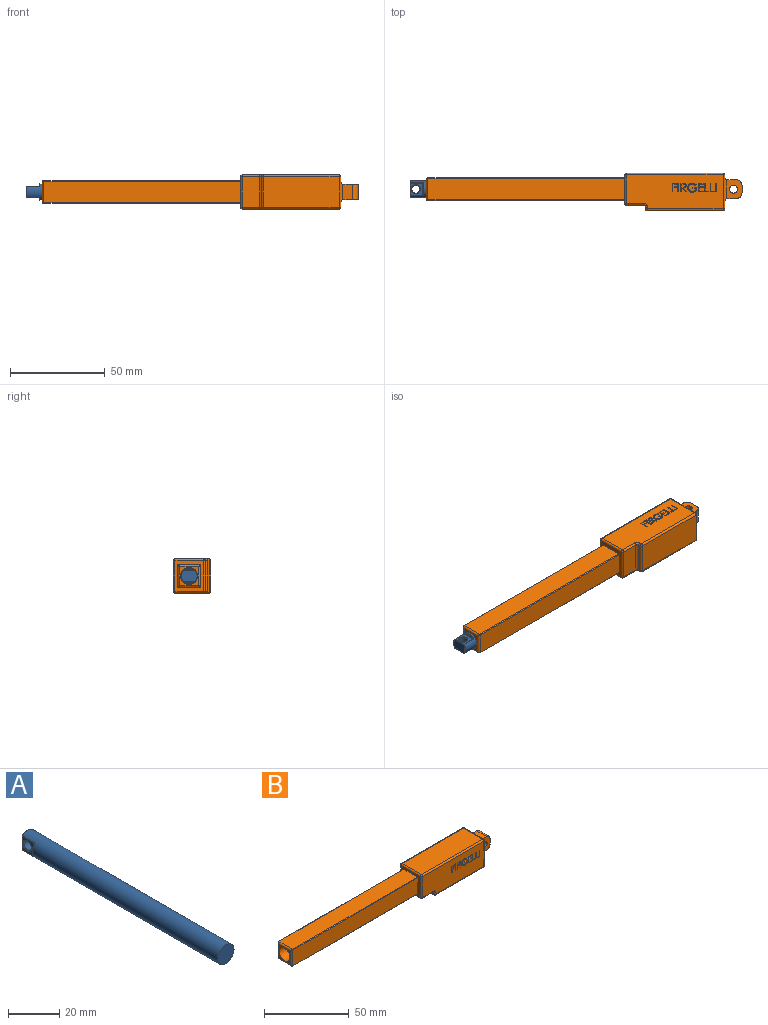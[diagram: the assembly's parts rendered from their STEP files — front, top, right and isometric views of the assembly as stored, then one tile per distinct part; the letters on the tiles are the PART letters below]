
ASSEMBLY  parts=2 mates=1
PART A: 30 faces, bbox 9.7x110x9.7 mm
  f0: cylinder r=4.5mm len=109.7mm, axis (0,-1,0), area 2992.2mm2, adj f2,f8,f9,f11,f13,f14,f15,f17
  f1: plane 8.4x5.4mm, normal (0,1,0), area 42mm2, adj f15,f16,f23,f24
  f2: plane 9x9mm, normal (0,-1,0), area 63.6mm2, adj f0
  f3: plane 6.43x6.4mm, normal (1,0,0), area 22.7mm2, adj f9,f10,f16,f17,f29
  f4: plane 5.2x0.9mm, normal (0,1,0), area 3.2mm2, adj f10,f11
  f5: plane 5.2x0.9mm, normal (0,1,0), area 3.2mm2, adj f21,f22
  f6: plane 6.43x6.4mm, normal (-1,0,0), area 22.7mm2, adj f14,f22,f23,f27,f28
  f7: cylinder r=2.12mm len=5.4mm, axis (1,0,0), area 72.1mm2, adj f28,f29
  f8: bspline ~0.85x0.71mm, area 0.3mm2, adj f0,f9,f10,f11
  f9: cylinder r=0.3mm len=6.4mm, axis (0,-1,0), area 1.7mm2, adj f0,f3,f8,f12
  f10: cylinder r=0.3mm len=6.43mm, axis (0,0,1), area 2.8mm2, adj f3,f4,f8,f13
  f11: torus R=4.2mm, axis (0,1,0), area 2.8mm2, adj f0,f4,f8,f13
  f12: sphere r=0.3mm, area 0.1mm2, adj f9,f15,f16
  f13: bspline ~1.14x0.87mm, area 0.3mm2, adj f0,f10,f11,f17
  f14: cylinder r=0.3mm len=6.4mm, axis (0,-1,0), area 1.7mm2, adj f0,f6,f18,f19
  f15: torus R=4.2mm, axis (0,1,0), area 2.9mm2, adj f0,f1,f12,f19
  f16: cylinder r=0.3mm len=6.43mm, axis (0,0,-1), area 3mm2, adj f1,f3,f12,f20
  f17: cylinder r=0.3mm len=6.4mm, axis (0,-1,0), area 1.7mm2, adj f0,f3,f13,f20
  f18: bspline ~1.14x0.87mm, area 0.3mm2, adj f0,f14,f21,f22
  f19: sphere r=0.3mm, area 0.1mm2, adj f14,f15,f23
  f20: sphere r=0.3mm, area 0.1mm2, adj f16,f17,f24
  f21: torus R=4.2mm, axis (0,1,0), area 2.8mm2, adj f0,f5,f18,f25
  f22: cylinder r=0.3mm len=6.43mm, axis (0,0,-1), area 2.8mm2, adj f5,f6,f18,f25
  f23: cylinder r=0.3mm len=6.43mm, axis (0,0,1), area 3mm2, adj f1,f6,f19,f26
  f24: torus R=4.2mm, axis (0,1,0), area 2.9mm2, adj f0,f1,f20,f26
  f25: bspline ~0.85x0.71mm, area 0.3mm2, adj f0,f21,f22,f27
  f26: sphere r=0.3mm, area 0.1mm2, adj f23,f24,f27
  f27: cylinder r=0.3mm len=6.4mm, axis (0,-1,0), area 1.7mm2, adj f0,f6,f25,f26
  f28: torus R=2.43mm, axis (-1,0,0), area 6.6mm2, adj f6,f7
  f29: torus R=2.43mm, axis (1,0,0), area 6.6mm2, adj f3,f7
PART B: 229 faces, bbox 167x18.2x20 mm
  f0: plane 51x18mm, normal (0,1,0), area 854.5mm2, adj f25,f31,f39,f40,f41,f43,f50,f149
  f1: plane 51x18mm, normal (0,-1,0), area 854.5mm2, adj f28,f36,f46,f53,f54,f55,f57,f69
  f2: cylinder r=1mm len=10mm, axis (0,-1,0), area 13.7mm2, adj f3,f19,f27,f30
  f3: plane 8x5mm, normal (0,0,1), area 40mm2, adj f2,f4,f26,f29
  f4: cylinder r=3mm len=8mm, axis (0,-1,0), area 37.7mm2, adj f3,f5,f26,f29
  f5: plane 8x4mm, normal (1,0,0), area 32mm2, adj f4,f6,f26,f29
  f6: cylinder r=3mm len=8mm, axis (0,-1,0), area 37.7mm2, adj f5,f7,f26,f29
  f7: plane 8x5mm, normal (0,0,-1), area 40mm2, adj f6,f8,f26,f29
  f8: cylinder r=1mm len=10mm, axis (0,-1,0), area 13.7mm2, adj f7,f19,f27,f30
  f9: cylinder r=1mm len=16mm, axis (0,-1,0), area 25.1mm2, adj f19,f20,f44,f58
  f10: cylinder r=1mm len=16mm, axis (0,-1,0), area 25.1mm2, adj f16,f24,f38,f52
  f11: plane 104x11.4mm, normal (0,0,-1), area 1185.6mm2, adj f12,f16,f65,f67
  f12: cylinder r=1mm len=11.4mm, axis (0,-1,0), area 17.1mm2, adj f11,f13,f66,f68
  f13: plane 10x10mm, normal (-1,0,0), area 36.4mm2, adj f12,f14,f33,f34,f59
  f14: cylinder r=1mm len=11.4mm, axis (0,-1,0), area 17.1mm2, adj f13,f15,f62,f64
  f15: plane 104x11.4mm, normal (0,0,1), area 1185.6mm2, adj f14,f16,f61,f63
  f16: plane 16x15mm, normal (-1,0,0), area 96.1mm2, adj f10,f11,f15,f17,f31,f32,f35,f36
  f17: cylinder r=1mm len=16mm, axis (0,-1,0), area 25.1mm2, adj f16,f18,f45,f51
  f18: plane 51x16mm, normal (0,0,1), area 816mm2, adj f17,f46,f48,f50
  f19: plane 18x16mm, normal (1,0,0), area 168mm2, adj f2,f8,f9,f25,f27,f28,f30,f48
  f20: plane 40x16mm, normal (0,0,-1), area 640mm2, adj f9,f21,f43,f57
  f21: cylinder r=1mm len=16mm, axis (0,-1,0), area 25.1mm2, adj f20,f22,f42,f56
  f22: plane 16x1mm, normal (-1,0,0), area 16mm2, adj f21,f23,f41,f55
  f23: cylinder r=1mm len=16mm, axis (0,-1,0), area 25.1mm2, adj f22,f24,f40,f54
  f24: plane 16x9mm, normal (0,0,-1), area 144mm2, adj f10,f23,f39,f53
  f25: cylinder r=1mm len=18mm, axis (0,0,1), area 28.3mm2, adj f0,f19,f44,f49
  f26: plane 10x8mm, normal (0,1,0), area 62mm2, adj f3,f4,f5,f6,f7,f27,f37
  f27: cylinder r=1mm len=12mm, axis (0,0,1), area 16.8mm2, adj f2,f8,f19,f26
  f28: cylinder r=1mm len=18mm, axis (0,0,1), area 28.3mm2, adj f1,f19,f47,f58
  f29: plane 10x8mm, normal (0,-1,0), area 62mm2, adj f3,f4,f5,f6,f7,f30,f37
  f30: cylinder r=1mm len=12mm, axis (0,0,1), area 16.8mm2, adj f2,f8,f19,f29
  f31: cylinder r=1mm len=15mm, axis (0,0,1), area 23.6mm2, adj f0,f16,f38,f51
  f32: plane 104x11.4mm, normal (0,1,0), area 1185.6mm2, adj f16,f33,f63,f67
  f33: cylinder r=1mm len=11.4mm, axis (0,0,1), area 17.1mm2, adj f13,f32,f64,f68
  f34: cylinder r=1mm len=11.4mm, axis (0,0,1), area 17.1mm2, adj f13,f35,f62,f66
  f35: plane 104x11.4mm, normal (0,-1,0), area 1185.6mm2, adj f16,f34,f61,f65
  f36: cylinder r=1mm len=15mm, axis (0,0,1), area 23.6mm2, adj f1,f16,f45,f52
  f37: cylinder r=2.12mm len=8mm, axis (0,-1,0), area 106.8mm2, adj f26,f29
  f38: sphere r=1mm, area 1.6mm2, adj f10,f31,f39
  f39: cylinder r=1mm len=9mm, axis (-1,0,0), area 14.1mm2, adj f0,f24,f38,f40
  f40: torus R=2mm, axis (0,-1,0), area 3.4mm2, adj f0,f23,f39,f41
  f41: cylinder r=1mm len=1mm, axis (0,0,1), area 1.6mm2, adj f0,f22,f40,f42
  f42: sphere r=1mm, area 1.6mm2, adj f21,f41,f43
  f43: cylinder r=1mm len=40mm, axis (-1,0,0), area 62.8mm2, adj f0,f20,f42,f44
  f44: sphere r=1mm, area 1.6mm2, adj f9,f25,f43
  f45: sphere r=1mm, area 1.6mm2, adj f17,f36,f46
  f46: cylinder r=1mm len=51mm, axis (-1,0,0), area 80.1mm2, adj f1,f18,f45,f47
  f47: sphere r=1mm, area 1.6mm2, adj f28,f46,f48
  f48: cylinder r=1mm len=16mm, axis (0,-1,0), area 25.1mm2, adj f18,f19,f47,f49
  f49: sphere r=1mm, area 1.6mm2, adj f25,f48,f50
  f50: cylinder r=1mm len=51mm, axis (1,0,0), area 80.1mm2, adj f0,f18,f49,f51
  f51: sphere r=1mm, area 1.6mm2, adj f17,f31,f50
  f52: sphere r=1mm, area 1.6mm2, adj f10,f36,f53
  f53: cylinder r=1mm len=9mm, axis (1,0,0), area 14.1mm2, adj f1,f24,f52,f54
  f54: torus R=2mm, axis (0,-1,0), area 3.4mm2, adj f1,f23,f53,f55
  f55: cylinder r=1mm len=1mm, axis (0,0,-1), area 1.6mm2, adj f1,f22,f54,f56
  f56: sphere r=1mm, area 1.6mm2, adj f21,f55,f57
  f57: cylinder r=1mm len=40mm, axis (1,0,0), area 62.8mm2, adj f1,f20,f56,f58
  f58: sphere r=1mm, area 1.6mm2, adj f9,f28,f57
  f59: cylinder r=4.5mm len=50mm, axis (-1,0,0), area 1413.7mm2, adj f13,f60
  f60: plane 9x9mm, normal (-1,0,0), area 63.6mm2, adj f59
  f61: cylinder r=0.3mm len=104mm, axis (1,0,0), area 49mm2, adj f15,f16,f35,f62
  f62: bspline ~1.17x1mm, area 0.5mm2, adj f14,f34,f61
  f63: cylinder r=0.3mm len=104mm, axis (-1,0,0), area 49mm2, adj f15,f16,f32,f64
  f64: bspline ~1.17x1mm, area 0.5mm2, adj f14,f33,f63
  f65: cylinder r=0.3mm len=104mm, axis (-1,0,0), area 49mm2, adj f11,f16,f35,f66
  f66: bspline ~1.04x1mm, area 0.5mm2, adj f12,f34,f65
  f67: cylinder r=0.3mm len=104mm, axis (1,0,0), area 49mm2, adj f11,f16,f32,f68
  f68: bspline ~1.17x1mm, area 0.5mm2, adj f12,f33,f67
  f69: plane 4.5x0.1mm, normal (-1,0,0), area 0.5mm2, adj f1,f70,f72,f73
  f70: plane 0.4x0.1mm, normal (0,0,-1), area 0mm2, adj f1,f69,f71,f73
  f71: plane 4.5x0.1mm, normal (1,0,0), area 0.5mm2, adj f1,f70,f72,f73
  f72: plane 0.4x0.1mm, normal (0,0,1), area 0mm2, adj f1,f69,f71,f73
  f73: plane 4.5x0.4mm, normal (0,-1,0), area 1.8mm2, adj f69,f70,f71,f72
  f74: plane 4.5x0.1mm, normal (-1,0,0), area 0.5mm2, adj f1,f75,f79,f80
  f75: plane 2.13x0.1mm, normal (0,0,-1), area 0.2mm2, adj f1,f74,f76,f80
  f76: plane 0.46x0.1mm, normal (1,0,0), area 0mm2, adj f1,f75,f77,f80
  f77: plane 1.73x0.1mm, normal (0,0,1), area 0.2mm2, adj f1,f76,f78,f80
  f78: plane 4.04x0.1mm, normal (1,0,0), area 0.4mm2, adj f1,f77,f79,f80
  f79: plane 0.4x0.1mm, normal (0,0,1), area 0mm2, adj f1,f74,f78,f80
  f80: plane 4.5x2.13mm, normal (0,-1,0), area 2.6mm2, adj f74,f75,f76,f77,f78,f79
  f81: plane 4.5x0.1mm, normal (-1,0,0), area 0.5mm2, adj f1,f82,f86,f87
  f82: plane 2.13x0.1mm, normal (0,0,-1), area 0.2mm2, adj f1,f81,f83,f87
  f83: plane 0.46x0.1mm, normal (1,0,0), area 0mm2, adj f1,f82,f84,f87
  f84: plane 1.73x0.1mm, normal (0,0,1), area 0.2mm2, adj f1,f83,f85,f87
  f85: plane 4.04x0.1mm, normal (1,0,0), area 0.4mm2, adj f1,f84,f86,f87
  f86: plane 0.4x0.1mm, normal (0,0,1), area 0mm2, adj f1,f81,f85,f87
  f87: plane 4.5x2.13mm, normal (0,-1,0), area 2.6mm2, adj f81,f82,f83,f84,f85,f86
  f88: plane 4.5x0.1mm, normal (-1,0,0), area 0.5mm2, adj f1,f89,f99,f100
  f89: plane 2.54x0.1mm, normal (0,0,-1), area 0.3mm2, adj f1,f88,f90,f100
  f90: plane 0.46x0.1mm, normal (1,0,0), area 0mm2, adj f1,f89,f91,f100
  f91: plane 2.13x0.1mm, normal (0,0,1), area 0.2mm2, adj f1,f90,f92,f100
  f92: plane 1.73x0.1mm, normal (1,0,0), area 0.2mm2, adj f1,f91,f93,f100
  f93: plane 2.13x0.1mm, normal (0,0,-1), area 0.2mm2, adj f1,f92,f94,f100
  f94: plane 0.46x0.1mm, normal (1,0,0), area 0mm2, adj f1,f93,f95,f100
  f95: plane 2.13x0.1mm, normal (0,0,1), area 0.2mm2, adj f1,f94,f96,f100
  f96: plane 1.38x0.1mm, normal (1,0,0), area 0.1mm2, adj f1,f95,f97,f100
  f97: plane 2.13x0.1mm, normal (0,0,-1), area 0.2mm2, adj f1,f96,f98,f100
  f98: plane 0.46x0.1mm, normal (1,0,0), area 0mm2, adj f1,f97,f99,f100
  f99: plane 2.54x0.1mm, normal (0,0,1), area 0.3mm2, adj f1,f88,f98,f100
  f100: plane 4.5x2.54mm, normal (0,-1,0), area 4.8mm2, adj f88,f89,f90,f91,f92,f93,f94,f95
  f101: extruded ~2.02x0.88mm, area 0.2mm2, adj f1,f102,f113,f114
  f102: extruded ~2.42x2.36mm, area 0.4mm2, adj f1,f101,f103,f114
  f103: extruded ~1.52x0.55mm, area 0.2mm2, adj f1,f102,f104,f114
  f104: extruded ~1.95x0.85mm, area 0.2mm2, adj f1,f103,f105,f114
  f105: extruded ~2.31x2.23mm, area 0.4mm2, adj f1,f104,f106,f114
  f106: plane 1.9x0.1mm, normal (0,0,1), area 0.2mm2, adj f1,f105,f107,f114
  f107: plane 0.46x0.1mm, normal (-1,0,0), area 0mm2, adj f1,f106,f108,f114
  f108: plane 1.5x0.1mm, normal (0,0,-1), area 0.2mm2, adj f1,f107,f109,f114
  f109: extruded ~1.79x1.38mm, area 0.2mm2, adj f1,f108,f110,f114
  f110: extruded ~2.13x1.92mm, area 0.3mm2, adj f1,f109,f111,f114
  f111: extruded ~2x1.88mm, area 0.3mm2, adj f1,f110,f112,f114
  f112: extruded ~1.69x0.75mm, area 0.2mm2, adj f1,f111,f113,f114
  f113: plane 0.35x0.33mm, normal (0.69,0,-0.73), area 0mm2, adj f1,f101,f112,f114
  f114: plane 4.73x4.73mm, normal (0,-1,0), area 6.1mm2, adj f101,f102,f103,f104,f105,f106,f107,f108
  f115: plane 4.5x2.88mm, normal (0,-1,0), area 5.3mm2, adj f116,f117,f118,f119,f120,f121,f122,f123
  f116: plane 4.5x0.1mm, normal (-1,0,0), area 0.5mm2, adj f1,f115,f117,f126
  f117: plane 0.4x0.1mm, normal (0,0,-1), area 0mm2, adj f1,f115,f116,f118
  f118: plane 2.08x0.1mm, normal (1,0,0), area 0.2mm2, adj f1,f115,f117,f119
  f119: plane 0.33x0.1mm, normal (0,0,-1), area 0mm2, adj f1,f115,f118,f120
  f120: plane 2.08x1.65mm, normal (-0.78,0,-0.62), area 0.3mm2, adj f1,f115,f119,f121
  f121: plane 0.5x0.1mm, normal (0,0,-1), area 0mm2, adj f1,f115,f120,f122
  f122: plane 2.08x1.65mm, normal (0.78,0,0.62), area 0.3mm2, adj f1,f115,f121,f123
  f123: extruded ~1.6x1.22mm, area 0.2mm2, adj f1,f115,f122,f124
  f124: extruded ~1.14x0.91mm, area 0.2mm2, adj f1,f115,f123,f125
  f125: extruded ~1.02x0.1mm, area 0.1mm2, adj f1,f115,f124,f126
  f126: plane 0.9x0.1mm, normal (0,0,1), area 0.1mm2, adj f1,f115,f116,f125
  f127: plane 0.84x0.1mm, normal (0,0,-1), area 0.1mm2, adj f115,f128,f131,f132
  f128: plane 1.5x0.1mm, normal (1,0,0), area 0.2mm2, adj f115,f127,f129,f132
  f129: plane 0.82x0.1mm, normal (0.01,0,1), area 0.1mm2, adj f115,f128,f130,f132
  f130: extruded ~1.2x0.77mm, area 0.2mm2, adj f115,f129,f131,f132
  f131: extruded ~1.18x0.74mm, area 0.2mm2, adj f115,f127,f130,f132
  f132: plane 2.02x1.51mm, normal (0,-1,0), area 2.8mm2, adj f127,f128,f129,f130,f131
  f133: plane 4.5x0.1mm, normal (-1,0,0), area 0.5mm2, adj f1,f134,f136,f137
  f134: plane 0.4x0.1mm, normal (0,0,-1), area 0mm2, adj f1,f133,f135,f137
  f135: plane 4.5x0.1mm, normal (1,0,0), area 0.5mm2, adj f1,f134,f136,f137
  f136: plane 0.4x0.1mm, normal (0,0,1), area 0mm2, adj f1,f133,f135,f137
  f137: plane 4.5x0.4mm, normal (0,-1,0), area 1.8mm2, adj f133,f134,f135,f136
  f138: plane 4.5x0.1mm, normal (-1,0,0), area 0.5mm2, adj f1,f139,f147,f148
  f139: plane 0.4x0.1mm, normal (0,0,-1), area 0mm2, adj f1,f138,f140,f148
  f140: plane 2.19x0.1mm, normal (1,0,0), area 0.2mm2, adj f1,f139,f141,f148
  f141: plane 1.79x0.1mm, normal (0,0,-1), area 0.2mm2, adj f1,f140,f142,f148
  f142: plane 0.46x0.1mm, normal (1,0,0), area 0mm2, adj f1,f141,f143,f148
  f143: plane 1.79x0.1mm, normal (0,0,1), area 0.2mm2, adj f1,f142,f144,f148
  f144: plane 1.38x0.1mm, normal (1,0,0), area 0.1mm2, adj f1,f143,f145,f148
  f145: plane 1.79x0.1mm, normal (0,0,-1), area 0.2mm2, adj f1,f144,f146,f148
  f146: plane 0.46x0.1mm, normal (1,0,0), area 0mm2, adj f1,f145,f147,f148
  f147: plane 2.19x0.1mm, normal (0,0,1), area 0.2mm2, adj f1,f138,f146,f148
  f148: plane 4.5x2.19mm, normal (0,-1,0), area 3.5mm2, adj f138,f139,f140,f141,f142,f143,f144,f145
  f149: plane 4.5x0.1mm, normal (1,0,0), area 0.5mm2, adj f0,f150,f158,f159
  f150: plane 0.4x0.1mm, normal (0,0,-1), area 0mm2, adj f0,f149,f151,f159
  f151: plane 2.19x0.1mm, normal (-1,0,0), area 0.2mm2, adj f0,f150,f152,f159
  f152: plane 1.79x0.1mm, normal (0,0,-1), area 0.2mm2, adj f0,f151,f153,f159
  f153: plane 0.46x0.1mm, normal (-1,0,0), area 0mm2, adj f0,f152,f154,f159
  f154: plane 1.79x0.1mm, normal (0,0,1), area 0.2mm2, adj f0,f153,f155,f159
  f155: plane 1.38x0.1mm, normal (-1,0,0), area 0.1mm2, adj f0,f154,f156,f159
  f156: plane 1.79x0.1mm, normal (0,0,-1), area 0.2mm2, adj f0,f155,f157,f159
  f157: plane 0.46x0.1mm, normal (-1,0,0), area 0mm2, adj f0,f156,f158,f159
  f158: plane 2.19x0.1mm, normal (0,0,1), area 0.2mm2, adj f0,f149,f157,f159
  f159: plane 4.5x2.19mm, normal (0,1,0), area 3.5mm2, adj f149,f150,f151,f152,f153,f154,f155,f156
  f160: plane 4.5x0.1mm, normal (1,0,0), area 0.5mm2, adj f0,f161,f163,f164
  f161: plane 0.4x0.1mm, normal (0,0,-1), area 0mm2, adj f0,f160,f162,f164
  f162: plane 4.5x0.1mm, normal (-1,0,0), area 0.5mm2, adj f0,f161,f163,f164
  f163: plane 0.4x0.1mm, normal (0,0,1), area 0mm2, adj f0,f160,f162,f164
  f164: plane 4.5x0.4mm, normal (0,1,0), area 1.8mm2, adj f160,f161,f162,f163
  f165: plane 4.5x2.88mm, normal (0,1,0), area 5.3mm2, adj f166,f167,f168,f169,f170,f171,f172,f173
  f166: plane 4.5x0.1mm, normal (1,0,0), area 0.5mm2, adj f0,f165,f167,f176
  f167: plane 0.4x0.1mm, normal (0,0,-1), area 0mm2, adj f0,f165,f166,f168
  f168: plane 2.08x0.1mm, normal (-1,0,0), area 0.2mm2, adj f0,f165,f167,f169
  f169: plane 0.33x0.1mm, normal (0,0,-1), area 0mm2, adj f0,f165,f168,f170
  f170: plane 2.08x1.65mm, normal (0.78,0,-0.62), area 0.3mm2, adj f0,f165,f169,f171
  f171: plane 0.5x0.1mm, normal (0,0,-1), area 0mm2, adj f0,f165,f170,f172
  f172: plane 2.08x1.65mm, normal (-0.78,0,0.62), area 0.3mm2, adj f0,f165,f171,f173
  f173: extruded ~1.6x1.22mm, area 0.2mm2, adj f0,f165,f172,f174
  f174: extruded ~1.14x0.91mm, area 0.2mm2, adj f0,f165,f173,f175
  f175: extruded ~1.02x0.1mm, area 0.1mm2, adj f0,f165,f174,f176
  f176: plane 0.9x0.1mm, normal (0,0,1), area 0.1mm2, adj f0,f165,f166,f175
  f177: plane 0.84x0.1mm, normal (0,0,-1), area 0.1mm2, adj f165,f178,f181,f182
  f178: plane 1.5x0.1mm, normal (-1,0,0), area 0.2mm2, adj f165,f177,f179,f182
  f179: plane 0.82x0.1mm, normal (-0.01,0,1), area 0.1mm2, adj f165,f178,f180,f182
  f180: extruded ~1.2x0.77mm, area 0.2mm2, adj f165,f179,f181,f182
  f181: extruded ~1.18x0.74mm, area 0.2mm2, adj f165,f177,f180,f182
  f182: plane 2.02x1.51mm, normal (0,1,0), area 2.8mm2, adj f177,f178,f179,f180,f181
  f183: extruded ~2.02x0.88mm, area 0.2mm2, adj f0,f184,f195,f196
  f184: extruded ~2.42x2.36mm, area 0.4mm2, adj f0,f183,f185,f196
  f185: extruded ~1.52x0.55mm, area 0.2mm2, adj f0,f184,f186,f196
  f186: extruded ~1.95x0.85mm, area 0.2mm2, adj f0,f185,f187,f196
  f187: extruded ~2.31x2.23mm, area 0.4mm2, adj f0,f186,f188,f196
  f188: plane 1.9x0.1mm, normal (0,0,1), area 0.2mm2, adj f0,f187,f189,f196
  f189: plane 0.46x0.1mm, normal (1,0,0), area 0mm2, adj f0,f188,f190,f196
  f190: plane 1.5x0.1mm, normal (0,0,-1), area 0.2mm2, adj f0,f189,f191,f196
  f191: extruded ~1.79x1.38mm, area 0.2mm2, adj f0,f190,f192,f196
  f192: extruded ~2.13x1.92mm, area 0.3mm2, adj f0,f191,f193,f196
  f193: extruded ~2x1.88mm, area 0.3mm2, adj f0,f192,f194,f196
  f194: extruded ~1.69x0.75mm, area 0.2mm2, adj f0,f193,f195,f196
  f195: plane 0.35x0.33mm, normal (-0.69,0,-0.73), area 0mm2, adj f0,f183,f194,f196
  f196: plane 4.73x4.73mm, normal (0,1,0), area 6.1mm2, adj f183,f184,f185,f186,f187,f188,f189,f190
  f197: plane 4.5x0.1mm, normal (1,0,0), area 0.5mm2, adj f0,f198,f208,f209
  f198: plane 2.54x0.1mm, normal (0,0,-1), area 0.3mm2, adj f0,f197,f199,f209
  f199: plane 0.46x0.1mm, normal (-1,0,0), area 0mm2, adj f0,f198,f200,f209
  f200: plane 2.13x0.1mm, normal (0,0,1), area 0.2mm2, adj f0,f199,f201,f209
  f201: plane 1.73x0.1mm, normal (-1,0,0), area 0.2mm2, adj f0,f200,f202,f209
  f202: plane 2.13x0.1mm, normal (0,0,-1), area 0.2mm2, adj f0,f201,f203,f209
  f203: plane 0.46x0.1mm, normal (-1,0,0), area 0mm2, adj f0,f202,f204,f209
  f204: plane 2.13x0.1mm, normal (0,0,1), area 0.2mm2, adj f0,f203,f205,f209
  f205: plane 1.38x0.1mm, normal (-1,0,0), area 0.1mm2, adj f0,f204,f206,f209
  f206: plane 2.13x0.1mm, normal (0,0,-1), area 0.2mm2, adj f0,f205,f207,f209
  f207: plane 0.46x0.1mm, normal (-1,0,0), area 0mm2, adj f0,f206,f208,f209
  f208: plane 2.54x0.1mm, normal (0,0,1), area 0.3mm2, adj f0,f197,f207,f209
  f209: plane 4.5x2.54mm, normal (0,1,0), area 4.8mm2, adj f197,f198,f199,f200,f201,f202,f203,f204
  f210: plane 4.5x0.1mm, normal (1,0,0), area 0.5mm2, adj f0,f211,f215,f216
  f211: plane 2.13x0.1mm, normal (0,0,-1), area 0.2mm2, adj f0,f210,f212,f216
  f212: plane 0.46x0.1mm, normal (-1,0,0), area 0mm2, adj f0,f211,f213,f216
  f213: plane 1.73x0.1mm, normal (0,0,1), area 0.2mm2, adj f0,f212,f214,f216
  f214: plane 4.04x0.1mm, normal (-1,0,0), area 0.4mm2, adj f0,f213,f215,f216
  f215: plane 0.4x0.1mm, normal (0,0,1), area 0mm2, adj f0,f210,f214,f216
  f216: plane 4.5x2.13mm, normal (0,1,0), area 2.6mm2, adj f210,f211,f212,f213,f214,f215
  f217: plane 4.5x0.1mm, normal (1,0,0), area 0.5mm2, adj f0,f218,f222,f223
  f218: plane 2.13x0.1mm, normal (0,0,-1), area 0.2mm2, adj f0,f217,f219,f223
  f219: plane 0.46x0.1mm, normal (-1,0,0), area 0mm2, adj f0,f218,f220,f223
  f220: plane 1.73x0.1mm, normal (0,0,1), area 0.2mm2, adj f0,f219,f221,f223
  f221: plane 4.04x0.1mm, normal (-1,0,0), area 0.4mm2, adj f0,f220,f222,f223
  f222: plane 0.4x0.1mm, normal (0,0,1), area 0mm2, adj f0,f217,f221,f223
  f223: plane 4.5x2.13mm, normal (0,1,0), area 2.6mm2, adj f217,f218,f219,f220,f221,f222
  f224: plane 4.5x0.1mm, normal (1,0,0), area 0.5mm2, adj f0,f225,f227,f228
  f225: plane 0.4x0.1mm, normal (0,0,-1), area 0mm2, adj f0,f224,f226,f228
  f226: plane 4.5x0.1mm, normal (-1,0,0), area 0.5mm2, adj f0,f225,f227,f228
  f227: plane 0.4x0.1mm, normal (0,0,1), area 0mm2, adj f0,f224,f226,f228
  f228: plane 4.5x0.4mm, normal (0,1,0), area 1.8mm2, adj f224,f225,f226,f227
PLACE A rot(axis=(-0.58,0.58,0.58),120deg) t=(-21,0,0)mm
PLACE B rot(axis=(-1,0,0),90deg) t=(-4.5,8.5,0)mm
MATE slider B.f59 <-> A.f0  axis (-1,0,0) through (-162.5,0,0)mm
